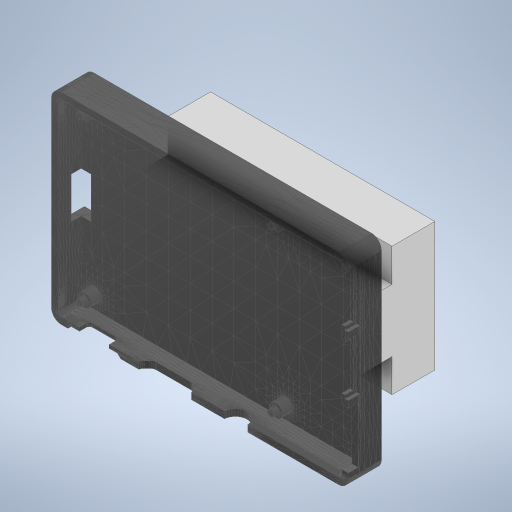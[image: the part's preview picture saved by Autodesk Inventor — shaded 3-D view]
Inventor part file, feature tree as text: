
AUTODESK INVENTOR PART (.ipt)
format: ipt  version: 2023 (Build 270158000, 158)  size: 620,032 bytes
history: native  units: mm
features: other x2, extrude x2, sketch x2
ambient origin geometry x8: Origin, YZ Plane, XZ Plane, XY Plane, X Axis, Y Axis, Z Axis, Center Point
bodies: Body1 (feature_tree)
feature tree (6):
  other  "bottom"
  extrude  "Extrusion4"  Depth=68.0mm
  extrude  "Extrusion5"  Depth=68.0mm
  sketch  "Sketch1"  dims[d0=68.0mm d1=47.0mm]
  sketch  "Sketch5"  dims[d30=30.0mm d31=0.0mm d32=14.0mm d33=14.0mm d34=11.0mm d35=10.0mm d36=11.0mm d37=10.0mm d38=13.0mm d39=13.0mm d40=68.0mm d41=0.0mm d42=0.5mm d43=0.872665mm]
  other  "MeshFeature1"
